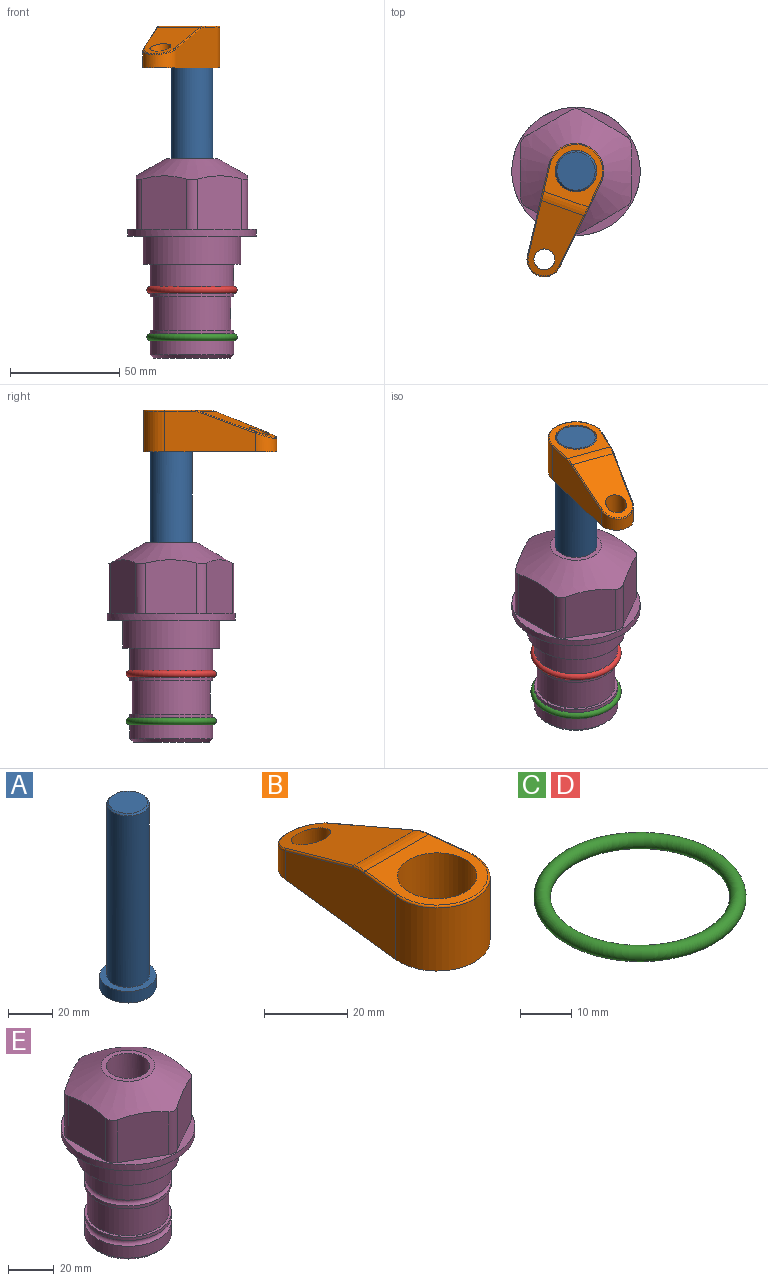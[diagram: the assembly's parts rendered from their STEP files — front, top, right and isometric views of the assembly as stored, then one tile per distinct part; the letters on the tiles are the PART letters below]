
ASSEMBLY  parts=5 mates=3
PART A: 6 faces, bbox 25.4x25.4x101.6 mm
  f0: plane 17.46x17.46mm, normal (0,0,1), area 239.5mm2, adj f5
  f1: plane 25.4x25.4mm, normal (0,0,-1), area 506.7mm2, adj f2
  f2: cylinder r=12.7mm len=25.4mm, axis (0,0,1), area 506.7mm2, adj f1,f3
  f3: plane 25.4x25.4mm, normal (0,0,1), area 221.7mm2, adj f2,f4
  f4: cylinder r=9.53mm len=94.46mm, axis (0,0,1), area 5653mm2, adj f3,f5
  f5: cone r=8.73mm half-angle=45deg, axis (0,0,-1), area 64.4mm2, adj f0,f4
PART B: 44 faces, bbox 27.5x64.5x19.1 mm
  f0: plane 2.3x0.95mm, normal (0,0,-1), area 1mm2, adj f25,f30,f34
  f1: plane 63.5x25.4mm, normal (0,0,-1), area 561.7mm2, adj f2,f3,f4,f5,f6,f7,f19,f20
  f2: cylinder r=12.7mm len=25.4mm, axis (0,0,-1), area 792.2mm2, adj f1,f3,f5,f13
  f3: plane 42.33x18.54mm, normal (0.99,0.11,0), area 647mm2, adj f1,f2,f4,f11,f12,f14
  f4: cylinder r=7.94mm len=15.78mm, axis (0,0,-1), area 158.6mm2, adj f1,f3,f5,f16
  f5: plane 42.33x18.54mm, normal (-0.99,0.11,0), area 647mm2, adj f1,f2,f4,f15,f17,f18
  f6: cylinder r=9.53mm len=19.05mm, axis (0,0,-1), area 1140.1mm2, adj f1,f8
  f7: cylinder r=4.76mm len=10.98mm, axis (0,0,-1), area 276.1mm2, adj f1,f9
  f8: plane 25.83x24.38mm, normal (0,0,1), area 262.2mm2, adj f6,f10,f11,f13,f15
  f9: plane 32.49x20.55mm, normal (0,0.34,0.94), area 489.9mm2, adj f7,f10,f14,f16,f18
  f10: cylinder r=12.7mm len=21.49mm, axis (-1,0,0), area 93.2mm2, adj f8,f9,f12,f17
  f11: cylinder r=0.51mm len=12.34mm, axis (0.11,-0.99,0), area 9.9mm2, adj f3,f8,f12,f13
  f12: bspline ~7.62x1.64mm, area 3.5mm2, adj f3,f10,f11,f14
  f13: torus R=12.19mm, axis (0,0,1), area 33.6mm2, adj f2,f8,f11,f15
  f14: cylinder r=0.51mm len=26.01mm, axis (0.1,-0.93,0.34), area 21.6mm2, adj f3,f9,f12,f16
  f15: cylinder r=0.51mm len=12.34mm, axis (0.11,0.99,0), area 9.9mm2, adj f5,f8,f13,f17
  f16: bspline ~15.78x7.05mm, area 15.7mm2, adj f4,f9,f14,f18
  f17: bspline ~7.62x1.64mm, area 3.5mm2, adj f5,f10,f15,f18
  f18: cylinder r=0.51mm len=26.01mm, axis (0.1,0.93,-0.34), area 21.6mm2, adj f5,f9,f16,f17
  f19: plane 21.6x14.29mm, normal (-0.99,-0.11,0), area 242.6mm2, adj f1,f26,f28,f34,f36,f38
  f20: plane 21.6x14.29mm, normal (0.99,-0.11,0), area 242.6mm2, adj f1,f27,f29,f37,f39,f41
  f21: cylinder r=12.7mm len=14.29mm, axis (0,0,-1), area 173.2mm2, adj f1,f26,f27,f30,f31,f33
  f22: cylinder r=7.94mm len=7.63mm, axis (0,0,-1), area 53.8mm2, adj f1,f28,f29,f42
  f23: plane 2.3x0.95mm, normal (0,0,-1), area 1mm2, adj f25,f33,f37
  f24: plane 17.94x12.32mm, normal (0,-0.34,-0.94), area 191.2mm2, adj f25,f38,f41,f42
  f25: cylinder r=9.53mm len=12.93mm, axis (-1,0,0), area 37.5mm2, adj f0,f23,f24,f31,f36,f39
  f26: cylinder r=1.59mm len=14.29mm, axis (0,0,-1), area 49mm2, adj f1,f19,f21,f32
  f27: cylinder r=1.59mm len=14.29mm, axis (0,0,-1), area 49mm2, adj f1,f20,f21,f35
  f28: cylinder r=1.59mm len=7.28mm, axis (0,0,-1), area 22.1mm2, adj f1,f19,f22,f40
  f29: cylinder r=1.59mm len=7.28mm, axis (0,0,-1), area 22.1mm2, adj f1,f20,f22,f43
  f30: torus R=14.29mm, axis (0,0,1), area 5.8mm2, adj f0,f21,f31,f32
  f31: bspline ~11.06x2.73mm, area 20.8mm2, adj f21,f25,f30,f33
  f32: sphere r=1.59mm, area 5.4mm2, adj f26,f30,f34
  f33: torus R=14.29mm, axis (0,0,1), area 5.8mm2, adj f21,f23,f31,f35
  f34: cylinder r=1.59mm len=1.68mm, axis (-0.11,0.99,0), area 2.4mm2, adj f0,f19,f32,f36
  f35: sphere r=1.59mm, area 5.4mm2, adj f27,f33,f37
  f36: bspline ~5.82x2.33mm, area 7.7mm2, adj f19,f25,f34,f38
  f37: cylinder r=1.59mm len=1.68mm, axis (0.11,0.99,0), area 2.4mm2, adj f20,f23,f35,f39
  f38: cylinder r=1.59mm len=18.33mm, axis (0.1,-0.93,0.34), area 46.7mm2, adj f19,f24,f36,f40
  f39: bspline ~5.82x2.33mm, area 7.7mm2, adj f20,f25,f37,f41
  f40: sphere r=1.59mm, area 3.6mm2, adj f28,f38,f42
  f41: cylinder r=1.59mm len=18.33mm, axis (0.1,0.93,-0.34), area 46.7mm2, adj f20,f24,f39,f43
  f42: bspline ~8.31x1.84mm, area 15.3mm2, adj f22,f24,f40,f43
  f43: sphere r=1.59mm, area 3.6mm2, adj f29,f41,f42
PART C: 1 faces, bbox 44.7x44.7x3.2 mm
  f0: torus R=19.05mm, axis (0,0,1), area 1193.9mm2
PART D: same geometry as C
PART E: 36 faces, bbox 58.7x58.7x91.2 mm
  f0: cylinder r=17.78mm len=35.56mm, axis (0,0,1), area 1670.8mm2, adj f23,f24,f31
  f1: cylinder r=19.05mm len=38.1mm, axis (0,0,1), area 1191.9mm2, adj f26,f27,f30
  f2: plane 58.66x58.66mm, normal (0,0,-1), area 1150.6mm2, adj f3,f28
  f3: cylinder r=29.33mm len=58.66mm, axis (0,0,-1), area 585.1mm2, adj f2,f4
  f4: plane 58.66x58.66mm, normal (0,0,1), area 475.9mm2, adj f3,f5,f6,f7,f8,f9,f10,f11
  f5: plane 24.5x20.32mm, normal (-0.5,0.87,0), area 562.8mm2, adj f4,f15,f16,f17
  f6: plane 24.5x20.32mm, normal (0.5,0.87,0), area 562.8mm2, adj f4,f14,f15,f17
  f7: plane 24.5x23.48mm, normal (1,0,0), area 562.8mm2, adj f4,f13,f14,f17
  f8: plane 24.5x20.32mm, normal (0.5,-0.87,0), area 562.8mm2, adj f4,f12,f13,f17
  f9: plane 24.5x20.32mm, normal (-0.5,-0.87,0), area 562.8mm2, adj f4,f11,f12,f17
  f10: plane 24.5x23.48mm, normal (-1,0,0), area 562.8mm2, adj f4,f11,f16,f17
  f11: cylinder r=5.08mm len=23.01mm, axis (0,0,-1), area 121.2mm2, adj f4,f9,f10,f17
  f12: cylinder r=5.08mm len=23.01mm, axis (0,0,-1), area 121.2mm2, adj f4,f8,f9,f17
  f13: cylinder r=5.08mm len=23.01mm, axis (0,0,-1), area 121.2mm2, adj f4,f7,f8,f17
  f14: cylinder r=5.08mm len=23.01mm, axis (0,0,-1), area 121.2mm2, adj f4,f6,f7,f17
  f15: cylinder r=5.08mm len=23.01mm, axis (0,0,-1), area 121.2mm2, adj f4,f5,f6,f17
  f16: cylinder r=5.08mm len=23.01mm, axis (0,0,-1), area 121.2mm2, adj f4,f5,f10,f17
  f17: cone r=11.73mm half-angle=60deg, axis (0,0,-1), area 2071.8mm2, adj f5,f6,f7,f8,f9,f10,f11,f12
  f18: plane 23.46x23.46mm, normal (0,0,1), area 147.4mm2, adj f17,f35
  f19: plane 34.93x34.93mm, normal (0,0,-1), area 958mm2, adj f29
  f20: cylinder r=19.05mm len=38.1mm, axis (0,0,1), area 760.1mm2, adj f21,f29
  f21: torus R=19.05mm, axis (0,0,1), area 565.3mm2, adj f20,f22
  f22: cylinder r=19.05mm len=38.1mm, axis (0,0,1), area 190mm2, adj f21,f23
  f23: plane 38.1x38.1mm, normal (0,0,1), area 146.9mm2, adj f0,f22
  f24: plane 38.1x38.1mm, normal (0,0,-1), area 146.9mm2, adj f0,f25
  f25: cylinder r=19.05mm len=38.1mm, axis (0,0,1), area 190mm2, adj f24,f26
  f26: torus R=19.05mm, axis (0,0,1), area 565.3mm2, adj f1,f25
  f27: plane 44.45x44.45mm, normal (0,0,-1), area 411.7mm2, adj f1,f28
  f28: cylinder r=22.23mm len=44.45mm, axis (0,0,1), area 1773.5mm2, adj f2,f27
  f29: cone r=19.05mm half-angle=45deg, axis (0,0,1), area 257.5mm2, adj f19,f20
  f30: cylinder r=3.17mm len=6.75mm, axis (-1,0,0), area 128mm2, adj f1,f33
  f31: cylinder r=3.17mm len=6.35mm, axis (-1,0,0), area 102.5mm2, adj f0,f33
  f32: plane 25.4x25.4mm, normal (0,0,1), area 506.7mm2, adj f33
  f33: cylinder r=12.7mm len=66.42mm, axis (0,0,-1), area 5236.2mm2, adj f30,f31,f32,f34
  f34: cone r=9.53mm half-angle=30deg, axis (0,0,-1), area 443.4mm2, adj f33,f35
  f35: cylinder r=9.53mm len=19.05mm, axis (0,0,-1), area 849mm2, adj f18,f34
PLACE A rot(axis=(0,0,-1),109.7deg) t=(0,0,22.46)mm
PLACE B rot(axis=(0,0,1),160.3deg) t=(0,0,77.07)mm
PLACE C t=(0,0,-21.59)mm
PLACE D at identity
PLACE E at identity fixed
MATE fastened C.f0 <-> E.f0  axis (0,0,1) through (0,0,-46.1)mm
MATE cylindrical A.f2 <-> E.f0  axis (0,0,1) through (0,0,48.1)mm
MATE fastened B.f2 <-> A.f2  axis (0,0,1) through (0,0,96.12)mm
